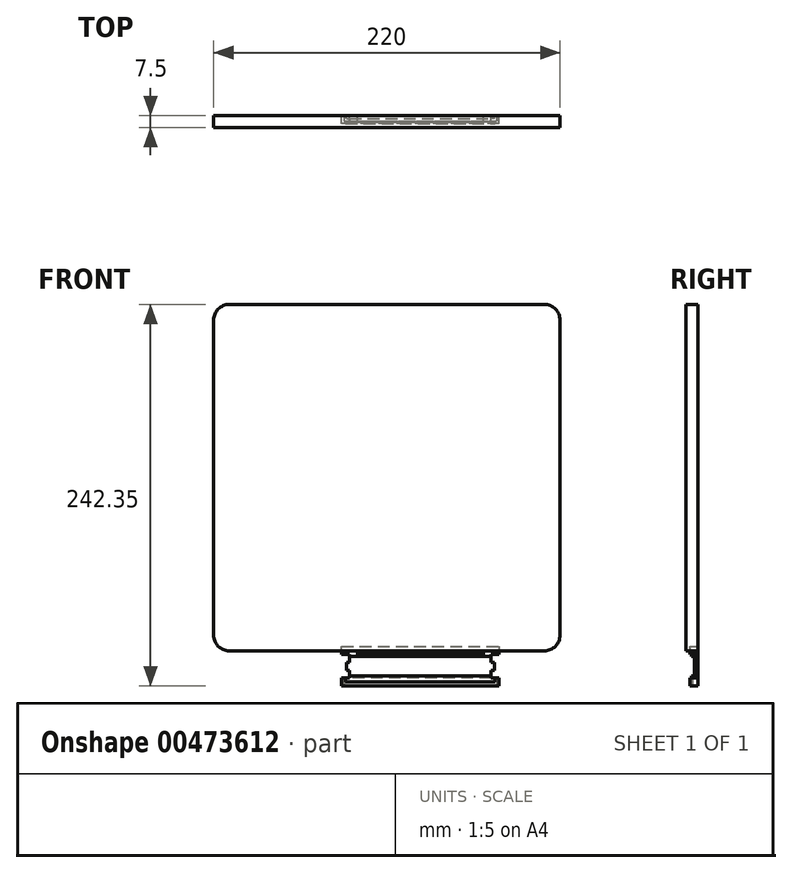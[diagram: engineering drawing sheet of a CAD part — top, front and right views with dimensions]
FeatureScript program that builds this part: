
annotation { "Feature Type Name" : "Feature", "Feature Type Description" : "" }
export const myFeature = defineFeature(function(context is Context, id is Id, definition is map)
    precondition{}
    {
        {
            var Q0;
            Q0=qCreatedBy(makeId("Front.planeOp"),FACE);
            var sketch = newSketch(context, id + "F0", { "sketchPlane" : qUnion([Q0])});
            skLineSegment(sketch, "E0.bottom", {"start": v(-166.56, 189.68) * mm, "end": v(33.44, 189.68) * mm});
            skLineSegment(sketch, "E0.top", {"start": v(-166.56, -30.32) * mm, "end": v(33.44, -30.32) * mm});
            skLineSegment(sketch, "E0.left", {"start": v(-176.56, 179.68) * mm, "end": v(-176.56, -20.32) * mm});
            skLineSegment(sketch, "E0.right", {"start": v(43.44, 179.68) * mm, "end": v(43.44, -20.32) * mm});
            skPoint(sketch, "E1.visualSharp", {"position": v(-176.56, 189.68) * mm});
            skArc(sketch, "E1.filletArc", {"start": v(-166.56, 189.68) * mm, "mid": v(-173.64, 186.75) * mm, "end": v(-176.56, 179.68) * mm});
            skPoint(sketch, "E2.visualSharp", {"position": v(-176.56, -30.32) * mm});
            skArc(sketch, "E2.filletArc", {"start": v(-176.56, -20.32) * mm, "mid": v(-173.64, -27.4) * mm, "end": v(-166.56, -30.32) * mm});
            skPoint(sketch, "E3.visualSharp", {"position": v(43.44, -30.32) * mm});
            skArc(sketch, "E3.filletArc", {"start": v(33.44, -30.32) * mm, "mid": v(40.5, -27.4) * mm, "end": v(43.44, -20.32) * mm});
            skPoint(sketch, "E4.visualSharp", {"position": v(43.44, 189.68) * mm});
            skArc(sketch, "E4.filletArc", {"start": v(43.44, 179.68) * mm, "mid": v(40.5, 186.75) * mm, "end": v(33.44, 189.68) * mm});
            skCircle(sketch, "E5", {"center": v(-116.56, 29.68) * mm, "radius": 5 * mm});
            skCircle(sketch, "E6.0.1.0", {"center": v(-116.56, 129.68) * mm, "radius": 5 * mm});
            skCircle(sketch, "E6.1.0.0", {"center": v(-16.56, 29.68) * mm, "radius": 5 * mm});
            skCircle(sketch, "E6.1.1.0", {"center": v(-16.56, 129.68) * mm, "radius": 5 * mm});
            skLineSegment(sketch, "E6.direction1", {"start": v(-116.56, 29.68) * mm, "end": v(-16.56, 29.68) * mm, "construction": true});
            skLineSegment(sketch, "E6.direction2", {"start": v(-116.56, 29.68) * mm, "end": v(-116.56, 129.68) * mm, "construction": true});
            skSolve(sketch);
        }
        {
            var Q0;
            Q0=makeQuery(id+"F0.imprint","IMPRINT",FACE,{"disambiguationData":[TD([[makeQuery(id+"F0.imprint","IMPRINT",EDGE,{"derivedFrom":sQuery(id+"F0.wireOp",EDGE,"E0.bottom")}),-1.0]])]});
            var Q1;
            Q1=makeQuery(id+"F0.imprint","IMPRINT",FACE,{"disambiguationData":[TD([[makeQuery(id+"F0.imprint","IMPRINT",EDGE,{"derivedFrom":sQuery(id+"F0.wireOp",EDGE,"E6.0.1.0")}),1.0]])]});
            var Q2;
            Q2=makeQuery(id+"F0.imprint","IMPRINT",FACE,{"disambiguationData":[TD([[makeQuery(id+"F0.imprint","IMPRINT",EDGE,{"derivedFrom":sQuery(id+"F0.wireOp",EDGE,"E6.1.1.0")}),1.0]])]});
            var Q3;
            Q3=makeQuery(id+"F0.imprint","IMPRINT",FACE,{"disambiguationData":[TD([[makeQuery(id+"F0.imprint","IMPRINT",EDGE,{"derivedFrom":sQuery(id+"F0.wireOp",EDGE,"E6.1.0.0")}),1.0]])]});
            var Q4;
            Q4=makeQuery(id+"F0.imprint","IMPRINT",FACE,{"disambiguationData":[TD([[makeQuery(id+"F0.imprint","IMPRINT",EDGE,{"derivedFrom":sQuery(id+"F0.wireOp",EDGE,"E5")}),1.0]])]});
            extrude(context, id + "F1", {"entities" : qUnion([Q0, Q1, Q2, Q3, Q4]), "depth" : 7.5 * mm});
        }
        {
            var Q0;
            Q0=qCreatedBy(makeId("Front.planeOp"),FACE);
            var sketch = newSketch(context, id + "F2", { "sketchPlane" : qUnion([Q0])});
            skLineSegment(sketch, "E7", {"start": v(-90.27, -52.67) * mm, "end": v(-95.27, -52.67) * mm});
            skLineSegment(sketch, "E8", {"start": v(-95.27, -52.67) * mm, "end": v(-95.27, -47.67) * mm});
            skLineSegment(sketch, "E9", {"start": v(-95.27, -47.67) * mm, "end": v(-90.27, -47.67) * mm});
            skLineSegment(sketch, "E10", {"start": v(-90.27, -47.67) * mm, "end": v(-90.27, -42.67) * mm});
            skLineSegment(sketch, "E11", {"start": v(-90.27, -42.67) * mm, "end": v(-92.27, -42.67) * mm});
            skLineSegment(sketch, "E12", {"start": v(-92.27, -42.67) * mm, "end": v(-92.27, -37.67) * mm});
            skLineSegment(sketch, "E13", {"start": v(-92.27, -37.67) * mm, "end": v(-90.27, -37.67) * mm});
            skLineSegment(sketch, "E14", {"start": v(-90.27, -37.67) * mm, "end": v(-90.27, -32.67) * mm});
            skLineSegment(sketch, "E15", {"start": v(-90.27, -32.67) * mm, "end": v(-95.27, -32.67) * mm});
            skLineSegment(sketch, "E16", {"start": v(-95.27, -32.67) * mm, "end": v(-95.27, -27.67) * mm});
            skLineSegment(sketch, "E17", {"start": v(-95.27, -27.67) * mm, "end": v(-90.27, -27.67) * mm});
            skLineSegment(sketch, "E18", {"start": v(-90.27, -27.67) * mm, "end": v(4.73, -27.67) * mm});
            skLineSegment(sketch, "E19", {"start": v(4.73, -27.67) * mm, "end": v(4.73, -32.67) * mm});
            skLineSegment(sketch, "E20", {"start": v(4.73, -32.67) * mm, "end": v(-0.27, -32.67) * mm});
            skLineSegment(sketch, "E21", {"start": v(-0.27, -32.67) * mm, "end": v(-0.27, -37.67) * mm});
            skLineSegment(sketch, "E22", {"start": v(-0.27, -37.67) * mm, "end": v(1.73, -37.67) * mm});
            skLineSegment(sketch, "E23", {"start": v(1.73, -37.67) * mm, "end": v(1.73, -42.67) * mm});
            skLineSegment(sketch, "E24", {"start": v(1.73, -42.67) * mm, "end": v(-0.27, -42.67) * mm});
            skLineSegment(sketch, "E25", {"start": v(-0.27, -42.67) * mm, "end": v(-0.27, -47.67) * mm});
            skLineSegment(sketch, "E26", {"start": v(-0.27, -47.67) * mm, "end": v(4.73, -47.67) * mm});
            skLineSegment(sketch, "E27", {"start": v(4.73, -47.67) * mm, "end": v(4.73, -52.67) * mm});
            skLineSegment(sketch, "E28", {"start": v(4.73, -52.67) * mm, "end": v(-90.27, -52.67) * mm});
            skLineSegment(sketch, "E29.bottom", {"start": v(-85.27, -30.17) * mm, "end": v(-5.27, -30.17) * mm});
            skLineSegment(sketch, "E29.top", {"start": v(-85.27, -32.67) * mm, "end": v(-5.27, -32.67) * mm});
            skLineSegment(sketch, "E29.left", {"start": v(-85.27, -30.17) * mm, "end": v(-85.27, -32.67) * mm});
            skLineSegment(sketch, "E29.right", {"start": v(-5.27, -30.17) * mm, "end": v(-5.27, -32.67) * mm});
            skSolve(sketch);
        }
        {
            var Q0;
            Q0=makeQuery(id+"F2.imprint","IMPRINT",FACE,{"disambiguationData":[TD([[makeQuery(id+"F2.imprint","IMPRINT",EDGE,{"derivedFrom":sQuery(id+"F2.wireOp",EDGE,"E7")}),-1.0]])]});
            extrude(context, id + "F3", {"entities" : qUnion([Q0]), "depth" : 5 * mm});
        }
        {
            var Q0;
            Q0=makeQuery(id+"F3.opExtrude","CAP_FACE",FACE,{"disambiguationData":[OSD([sQuery(id+"F2.wireOp",EDGE,"E7"),sQuery(id+"F2.wireOp",EDGE,"E8"),sQuery(id+"F2.wireOp",EDGE,"E9"),sQuery(id+"F2.wireOp",EDGE,"E10"),sQuery(id+"F2.wireOp",EDGE,"E11"),sQuery(id+"F2.wireOp",EDGE,"E12"),sQuery(id+"F2.wireOp",EDGE,"E13"),sQuery(id+"F2.wireOp",EDGE,"E14"),sQuery(id+"F2.wireOp",EDGE,"E15"),sQuery(id+"F2.wireOp",EDGE,"E16"),sQuery(id+"F2.wireOp",EDGE,"E17"),sQuery(id+"F2.wireOp",EDGE,"E18"),sQuery(id+"F2.wireOp",EDGE,"E19"),sQuery(id+"F2.wireOp",EDGE,"E20"),sQuery(id+"F2.wireOp",EDGE,"E21"),sQuery(id+"F2.wireOp",EDGE,"E22"),sQuery(id+"F2.wireOp",EDGE,"E23"),sQuery(id+"F2.wireOp",EDGE,"E24"),sQuery(id+"F2.wireOp",EDGE,"E25"),sQuery(id+"F2.wireOp",EDGE,"E26"),sQuery(id+"F2.wireOp",EDGE,"E27"),sQuery(id+"F2.wireOp",EDGE,"E28"),sQuery(id+"F2.wireOp",EDGE,"E29.bottom"),sQuery(id+"F2.wireOp",EDGE,"E29.top"),sQuery(id+"F2.wireOp",EDGE,"E29.left"),sQuery(id+"F2.wireOp",EDGE,"E29.right")])],"isStart":false});
            var sketch = newSketch(context, id + "F4", { "sketchPlane" : qUnion([Q0])});
            skLineSegment(sketch, "E30.bottom", {"start": v(-92.27, -33.92) * mm, "end": v(1.73, -33.92) * mm});
            skLineSegment(sketch, "E30.top", {"start": v(-92.27, -46.42) * mm, "end": v(1.73, -46.42) * mm});
            skLineSegment(sketch, "E30.left", {"start": v(-92.27, -33.92) * mm, "end": v(-92.27, -46.42) * mm});
            skLineSegment(sketch, "E30.right", {"start": v(1.73, -33.92) * mm, "end": v(1.73, -46.42) * mm});
            skLineSegment(sketch, "E31", {"start": v(-45.27, -27.67) * mm, "end": v(-45.27, -52.67) * mm, "construction": true});
            skSolve(sketch);
        }
        {
            var Q0;
            Q0 = qSketchRegion(id + "F4", true);
            extrude(context, id + "F5", {"entities" : qUnion([Q0]), "operationType" : NewBodyOperationType.REMOVE, "oppositeDirection" : true, "depth" : 3 * mm});
        }
        {
            var Q0;
            Q0=makeQuery(id+"F3.opExtrude","SWEPT_FACE",FACE,{"disambiguationData":[OSD([sQuery(id+"F2.wireOp",EDGE,"E7"),sQuery(id+"F2.wireOp",EDGE,"E28")])]});
            var sketch = newSketch(context, id + "F6", { "sketchPlane" : qUnion([Q0])});
            skLineSegment(sketch, "E32.bottom", {"start": v(-93.77, 0) * mm, "end": v(3.23, 0) * mm});
            skLineSegment(sketch, "E32.top", {"start": v(-93.77, 3.5) * mm, "end": v(3.23, 3.5) * mm});
            skLineSegment(sketch, "E32.left", {"start": v(-93.77, 0) * mm, "end": v(-93.77, 3.5) * mm});
            skLineSegment(sketch, "E32.right", {"start": v(3.23, 0) * mm, "end": v(3.23, 3.5) * mm});
            skSolve(sketch);
        }
        {
            var Q0;
            Q0 = qSketchRegion(id + "F6", true);
            extrude(context, id + "F7", {"entities" : qUnion([Q0]), "operationType" : NewBodyOperationType.REMOVE, "oppositeDirection" : true, "depth" : 5 * mm});
        }
        {
            var Q0;
            {var subQ0=sQuery(id+"F2.wireOp",EDGE,"E10");var subQ1=sQuery(id+"F2.wireOp",EDGE,"E9");var subQ2=sQuery(id+"F2.wireOp",EDGE,"E8");var subQ3=sQuery(id+"F2.wireOp",EDGE,"E28");var subQ4=sQuery(id+"F2.wireOp",EDGE,"E7");var subQ5=sQuery(id+"F2.wireOp",EDGE,"E25");var subQ6=sQuery(id+"F2.wireOp",EDGE,"E26");var subQ7=sQuery(id+"F2.wireOp",EDGE,"E27");Q0=makeQuery(id+"F5.boolean.opBoolean","SPLIT",FACE,{"disambiguationData":[TD([makeQuery(id+"F3.opExtrude","SWEPT_FACE",FACE,{"disambiguationData":[OSD([subQ2])]})])],"derivedFrom":makeQuery(id+"F3.opExtrude","CAP_FACE",FACE,{"disambiguationData":[OSD([subQ4,subQ2,subQ1,subQ0,sQuery(id+"F2.wireOp",EDGE,"E11"),sQuery(id+"F2.wireOp",EDGE,"E12"),sQuery(id+"F2.wireOp",EDGE,"E13"),sQuery(id+"F2.wireOp",EDGE,"E14"),sQuery(id+"F2.wireOp",EDGE,"E15"),sQuery(id+"F2.wireOp",EDGE,"E16"),sQuery(id+"F2.wireOp",EDGE,"E17"),sQuery(id+"F2.wireOp",EDGE,"E18"),sQuery(id+"F2.wireOp",EDGE,"E19"),sQuery(id+"F2.wireOp",EDGE,"E20"),sQuery(id+"F2.wireOp",EDGE,"E21"),sQuery(id+"F2.wireOp",EDGE,"E22"),sQuery(id+"F2.wireOp",EDGE,"E23"),sQuery(id+"F2.wireOp",EDGE,"E24"),subQ5,subQ6,subQ7,subQ3,sQuery(id+"F2.wireOp",EDGE,"E29.bottom"),sQuery(id+"F2.wireOp",EDGE,"E29.top"),sQuery(id+"F2.wireOp",EDGE,"E29.left"),sQuery(id+"F2.wireOp",EDGE,"E29.right")])],"isStart":false})});}
            var sketch = newSketch(context, id + "F8", { "sketchPlane" : qUnion([Q0])});
            skPoint(sketch, "E33.firstSnap0", {"position": v(4.73, -50.17) * mm});
            skPoint(sketch, "E33.firstSnap1", {"position": v(2.23, -47.67) * mm});
            skLineSegment(sketch, "E33.bottom", {"start": v(2.23, -50.17) * mm, "end": v(-92.77, -50.17) * mm});
            skLineSegment(sketch, "E33.top", {"start": v(2.23, -30.17) * mm, "end": v(-92.77, -30.17) * mm});
            skLineSegment(sketch, "E33.left", {"start": v(2.23, -50.17) * mm, "end": v(2.23, -30.17) * mm});
            skLineSegment(sketch, "E33.right", {"start": v(-92.77, -50.17) * mm, "end": v(-92.77, -30.17) * mm});
            skSolve(sketch);
        }
        {
            var Q0;
            Q0 = qSketchRegion(id + "F8", true);
            extrude(context, id + "F9", {"entities" : qUnion([Q0]), "operationType" : NewBodyOperationType.REMOVE, "oppositeDirection" : true, "depth" : 1 * mm});
        }
    });
